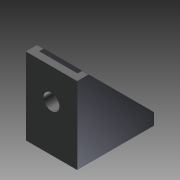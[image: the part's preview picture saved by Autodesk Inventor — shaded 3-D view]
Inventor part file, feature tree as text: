
AUTODESK INVENTOR PART (.ipt)
format: ipt  version: 2011 SP1 (Build 150282100, 282)  size: 205,824 bytes
history: native  units: mm
features: other x140, hole x44, sketch x11, extrude x9
ambient origin geometry x8: Origin, YZ Plane, XZ Plane, XY Plane, X Axis, Y Axis, Z Axis, Center Point
bodies: Solid1 (feature_tree)
feature tree (204):
  extrude  "Extrusion1"  Depth=15.0mm TaperAngle=0.0deg
  extrude  "Extrusion2"  Depth=2.25mm TaperAngle=0.0deg
  extrude  "Extrusion3"  Depth=1.0mm TaperAngle=0.0deg
  extrude  "Extrusion4"  Depth=1.0mm TaperAngle=0.0deg
  hole  "Hole1"  [1 undecoded]
  hole  "Hole2"  [1 undecoded]
  extrude  "Extrusion5"  [1 undecoded]
  extrude  "Extrusion6"  [1 undecoded]
  extrude  "Extrusion7"  [1 undecoded]
  extrude  "Extrusion8"  [1 undecoded]
  extrude  "Extrusion9"  [1 undecoded]
  other  "SD6_50_1_XY"
  other  "SD6_50_1_YZ"
  other  "SD6_50_1_ZX"
  other  "SD6_50_1_X"
  other  "SD6_50_1_Y"
  other  "SD6_50_1_Z"
  other  "SD6_50_1_Center"
  other  "SD6_50_2_XY"
  other  "SD6_50_2_YZ"
  other  "SD6_50_2_ZX"
  other  "SD6_50_2_X"
  other  "SD6_50_2_Y"
  other  "SD6_50_2_Z"
  other  "SD6_50_2_Center"
  other  "SD6_50_3_XY"
  other  "SD6_50_3_YZ"
  other  "SD6_50_3_ZX"
  other  "SD6_50_3_X"
  other  "SD6_50_3_Y"
  other  "SD6_50_3_Z"
  other  "SD6_50_3_Center"
  other  "SD6_50_4_XY"
  other  "SD6_50_4_YZ"
  other  "SD6_50_4_ZX"
  other  "SD6_50_4_X"
  other  "SD6_50_4_Y"
  other  "SD6_50_4_Z"
  other  "SD6_50_4_Center"
  other  "a10_to_bolt_XY"
  other  "a10_to_bolt_YZ"
  other  "a10_to_bolt_ZX"
  other  "a10_to_bolt_X"
  other  "a10_to_bolt_Y"
  other  "a10_to_bolt_Z"
  other  "a10_to_bolt_Center"
  other  "a11_to_bolt_XY"
  other  "a11_to_bolt_YZ"
  other  "a11_to_bolt_ZX"
  other  "a11_to_bolt_X"
  other  "a11_to_bolt_Y"
  other  "a11_to_bolt_Z"
  other  "a11_to_bolt_Center"
  other  "a12_to_bolt_XY"
  other  "a12_to_bolt_YZ"
  other  "a12_to_bolt_ZX"
  other  "a12_to_bolt_X"
  other  "a12_to_bolt_Y"
  other  "a12_to_bolt_Z"
  other  "a12_to_bolt_Center"
  other  "a13_to_bolt_XY"
  other  "a13_to_bolt_YZ"
  other  "a13_to_bolt_ZX"
  other  "a13_to_bolt_X"
  other  "a13_to_bolt_Y"
  other  "a13_to_bolt_Z"
  other  "a13_to_bolt_Center"
  other  "a14_to_bolt_XY"
  other  "a14_to_bolt_YZ"
  other  "a14_to_bolt_ZX"
  other  "a14_to_bolt_X"
  other  "a14_to_bolt_Y"
  other  "a14_to_bolt_Z"
  other  "a14_to_bolt_Center"
  other  "a1_to_bolt_XY"
  other  "a1_to_bolt_YZ"
  other  "a1_to_bolt_ZX"
  other  "a1_to_bolt_X"
  other  "a1_to_bolt_Y"
  other  "a1_to_bolt_Z"
  other  "a1_to_bolt_Center"
  other  "a2_to_bolt_XY"
  other  "a2_to_bolt_YZ"
  other  "a2_to_bolt_ZX"
  other  "a2_to_bolt_X"
  other  "a2_to_bolt_Y"
  other  "a2_to_bolt_Z"
  other  "a2_to_bolt_Center"
  other  "a3_to_bolt_XY"
  other  "a3_to_bolt_YZ"
  other  "a3_to_bolt_ZX"
  other  "a3_to_bolt_X"
  other  "a3_to_bolt_Y"
  other  "a3_to_bolt_Z"
  other  "a3_to_bolt_Center"
  other  "a4_to_bolt_XY"
  other  "a4_to_bolt_YZ"
  other  "a4_to_bolt_ZX"
  other  "a4_to_bolt_X"
  other  "a4_to_bolt_Y"
  other  "a4_to_bolt_Z"
  other  "a4_to_bolt_Center"
  other  "a55_to_bolt_XY"
  other  "a55_to_bolt_YZ"
  other  "a55_to_bolt_ZX"
  other  "a55_to_bolt_X"
  other  "a55_to_bolt_Y"
  other  "a55_to_bolt_Z"
  other  "a55_to_bolt_Center"
  other  "a5_to_bolt_XY"
  other  "a5_to_bolt_YZ"
  other  "a5_to_bolt_ZX"
  other  "a5_to_bolt_X"
  other  "a5_to_bolt_Y"
  other  "a5_to_bolt_Z"
  other  "a5_to_bolt_Center"
  other  "a6_to_bolt_XY"
  other  "a6_to_bolt_YZ"
  other  "a6_to_bolt_ZX"
  other  "a6_to_bolt_X"
  other  "a6_to_bolt_Y"
  other  "a6_to_bolt_Z"
  other  "a6_to_bolt_Center"
  other  "a7_to_bolt_XY"
  other  "a7_to_bolt_YZ"
  other  "a7_to_bolt_ZX"
  other  "a7_to_bolt_X"
  other  "a7_to_bolt_Y"
  other  "a7_to_bolt_Z"
  other  "a7_to_bolt_Center"
  other  "a8_to_bolt_XY"
  other  "a8_to_bolt_YZ"
  other  "a8_to_bolt_ZX"
  other  "a8_to_bolt_X"
  other  "a8_to_bolt_Y"
  other  "a8_to_bolt_Z"
  other  "a8_to_bolt_Center"
  other  "a9_to_bolt_XY"
  other  "a9_to_bolt_YZ"
  other  "a9_to_bolt_ZX"
  other  "a9_to_bolt_X"
  other  "a9_to_bolt_Y"
  other  "a9_to_bolt_Z"
  other  "a9_to_bolt_Center"
  other  "bracket_to_dummy_XY"
  other  "bracket_to_dummy_YZ"
  other  "bracket_to_dummy_ZX"
  other  "bracket_to_dummy_X"
  other  "bracket_to_dummy_Y"
  other  "bracket_to_dummy_Z"
  other  "bracket_to_dummy_Center"
  hole  "hole_x1_bolt_XY"  [1 undecoded]
  hole  "hole_x1_bolt_YZ"  [1 undecoded]
  hole  "hole_x1_bolt_ZX"  [1 undecoded]
  hole  "hole_x1_bolt_X"  [1 undecoded]
  hole  "hole_x1_bolt_Y"  [1 undecoded]
  hole  "hole_x1_bolt_Z"  [1 undecoded]
  hole  "hole_x1_bolt_Center"  [1 undecoded]
  hole  "holex2_to_bolt_XY"  [1 undecoded]
  hole  "holex2_to_bolt_YZ"  [1 undecoded]
  hole  "holex2_to_bolt_ZX"  [1 undecoded]
  hole  "holex2_to_bolt_X"  [1 undecoded]
  hole  "holex2_to_bolt_Y"  [1 undecoded]
  hole  "holex2_to_bolt_Z"  [1 undecoded]
  hole  "holex2_to_bolt_Center"  [1 undecoded]
  hole  "holex3_to_bolt_XY"  [1 undecoded]
  hole  "holex3_to_bolt_YZ"  [1 undecoded]
  hole  "holex3_to_bolt_ZX"  [1 undecoded]
  hole  "holex3_to_bolt_X"  [1 undecoded]
  hole  "holex3_to_bolt_Y"  [1 undecoded]
  hole  "holex3_to_bolt_Z"  [1 undecoded]
  hole  "holex3_to_bolt_Center"  [1 undecoded]
  hole  "holex4_to_bolt_XY"  [1 undecoded]
  hole  "holex4_to_bolt_YZ"  [1 undecoded]
  hole  "holex4_to_bolt_ZX"  [1 undecoded]
  hole  "holex4_to_bolt_X"  [1 undecoded]
  hole  "holex4_to_bolt_Y"  [1 undecoded]
  hole  "holex4_to_bolt_Z"  [1 undecoded]
  hole  "holex4_to_bolt_Center"  [1 undecoded]
  hole  "holex5_to_bolt_XY"  [1 undecoded]
  hole  "holex5_to_bolt_YZ"  [1 undecoded]
  hole  "holex5_to_bolt_ZX"  [1 undecoded]
  hole  "holex5_to_bolt_X"  [1 undecoded]
  hole  "holex5_to_bolt_Y"  [1 undecoded]
  hole  "holex5_to_bolt_Z"  [1 undecoded]
  hole  "holex5_to_bolt_Center"  [1 undecoded]
  hole  "holex6_to_bolt_XY"  [1 undecoded]
  hole  "holex6_to_bolt_YZ"  [1 undecoded]
  hole  "holex6_to_bolt_ZX"  [1 undecoded]
  hole  "holex6_to_bolt_X"  [1 undecoded]
  hole  "holex6_to_bolt_Y"  [1 undecoded]
  hole  "holex6_to_bolt_Z"  [1 undecoded]
  hole  "holex6_to_bolt_Center"  [1 undecoded]
  sketch  "Sketch_15"  dims[d24=1.0mm d25=0.0mm d26=1.0mm d27=0.0mm]
  sketch  "Sketch_16"  dims[d28=1.0mm d29=0.0mm d30=0.5mm d31=0.0mm]
  sketch  "Sketch_82"
  sketch  "Sketch_17"  dims[d32=0.0mm d33=0.0mm]
  sketch  "Sketch5"  dims[d8=6.2mm d9=6.0mm d10=4.0mm d11=2.0mm d12=90.0deg d13=5.5mm d14=0.0mm]
  sketch  "Sketch6"  dims[d15=6.2mm d16=6.0mm d17=4.0mm d18=2.0mm d19=90.0deg d20=4.5mm d21=0.0mm d22=1.0mm d23=0.0mm]
  sketch  "Sketch_1"  dims[d0=20.0mm d1=0.0mm d2=15.0mm d3=0.0mm]
  sketch  "Sketch_4"  dims[d4=15.0mm d5=0.0mm d6=2.25mm d7=0.0mm]
  sketch  "Sketch_72"
  sketch  "Sketch_73"
  sketch  "Sketch_86"
note: 49 required parameter values undecoded (feature->parameter linkage not recoverable at this tier; creation-order binding heuristic only, values carry confidence <= 0.55)
